# Revit family: WALL WASHER PRO 02_LV1210QW.30
name_source: partatom
category: Luminarias
units: mm (PartAtom-declared; Revit-internal decimal feet)

## family parameters
Compartido = No
Corte con vacíos al cargar = No
Cota de conector redondo = Diámetro de uso
Origen de luz = Sí
Punto de cálculo de habitación = No
Se basa en plano de trabajo = Sí
Siempre vertical = No
Tipo de pieza = Normal

## types (1)
- REFL_LV1210QW.30
    Archivo de red fotométrica = LV1210QW_30.ies
    Cambio de temperatura de color de luz atenuada = Curva de lámpara incandescente
    Comentarios de vataje = 90-277V
    Descripción = LUMINARIA TIPO REFLECTOR RGBW, WALL WASHER , CUERPO EN ALUMINIO FUNDIDO A PRESION CON UN PESO DE 12.4KG, CON 453MM DE LARGO POR 333MM DE ALTURA POR 114MM DE ESPESOR, CUENTA CON 12 LED TIPO CREE CON UN CONSUMO TOTAL DE 108W, 3800 LUMENES , RGBW, IP 66,  CABLE H07RN DE 0.5M, APERTURA DE 30 GRADOS EN STOCK, ALIMENTADA A 90-277V. REQUIERE ACCESORIOS.
    Elevación por defecto = 0 mm  [stored 0 ft]
    Fabricante = BRILLANT
    Filtro de color = 16777215
    Lámpara = CREE
    Modelo = LV1210QW.30
    Watt per fixture = 108
    Ángulo de inclinación = 30.00°

note: [stored X ft] marks values corroborated as IEEE doubles in the binary element streams (Revit-internal decimal feet)

## geometry (parser evidence)
native form markers: Blend x2
no freeform markers — native parametric forms only
